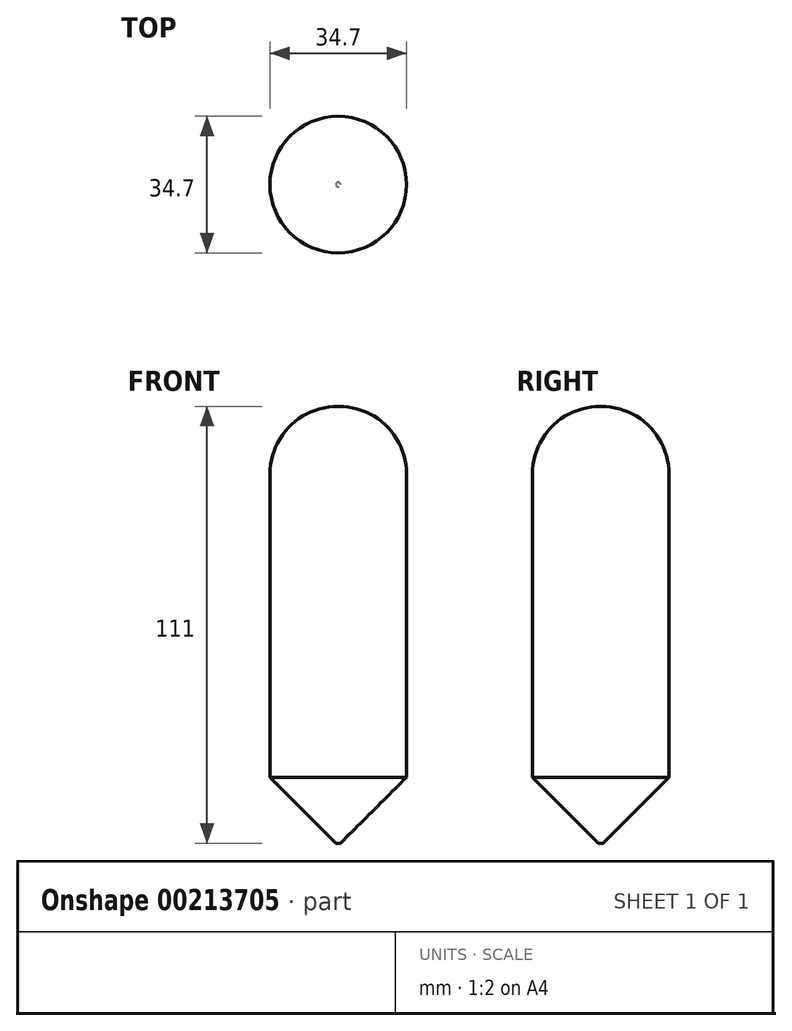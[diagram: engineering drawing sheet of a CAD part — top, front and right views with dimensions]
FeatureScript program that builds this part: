
annotation { "Feature Type Name" : "Feature", "Feature Type Description" : "" }
export const myFeature = defineFeature(function(context is Context, id is Id, definition is map)
    precondition{}
    {
        {
            var Q0;
            Q0=qCreatedBy(makeId("Top.planeOp"),FACE);
            var sketch = newSketch(context, id + "F0", { "sketchPlane" : qUnion([Q0])});
            skCircle(sketch, "E0", {"center": v(0, 0) * mm, "radius": 17.35 * mm});
            skSolve(sketch);
        }
        {
            var Q0;
            Q0=makeQuery(id+"F0.imprint","IMPRINT",FACE,{"disambiguationData":[TD([[makeQuery(id+"F0.imprint","IMPRINT",EDGE,{"derivedFrom":sQuery(id+"F0.wireOp",EDGE,"E0")}),1.0]])]});
            extrude(context, id + "F1", {"entities" : qUnion([Q0]), "depth" : 111 * mm});
        }
        {
            var Q0;
            Q0=makeQuery(id+"F1.opExtrude","CAP_FACE",FACE,{"disambiguationData":[OSD([sQuery(id+"F0.wireOp",EDGE,"E0")])],"isStart":false});
            fillet(context, id + "F2", {"entities" : qUnion([Q0]), "radius" : 17.17 * mm, "tangentPropagation" : true, "allowEdgeOverflow" : false});
        }
        {
            var Q0;
            Q0=makeQuery(id+"F1.opExtrude","CAP_FACE",FACE,{"disambiguationData":[OSD([sQuery(id+"F0.wireOp",EDGE,"E0")])],"isStart":true});
            chamfer(context, id + "F3", {"entities" : qUnion([Q0]), "width" : 16.76 * mm, "tangentPropagation" : true});
        }
    });
